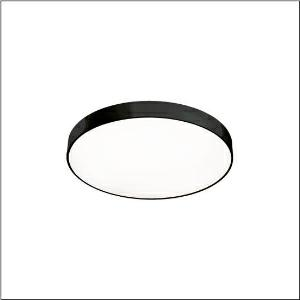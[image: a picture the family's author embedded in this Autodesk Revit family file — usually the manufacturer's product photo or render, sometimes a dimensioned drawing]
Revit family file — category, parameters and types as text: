
# Revit family: round_21_m_51mr36fd0321b
name_source: partatom
category: Lighting Fixtures
units: mm (PartAtom-declared; Revit-internal decimal feet)

## family parameters
Cut with Voids When Loaded = No
Host = Face
Light Source = No
Part Type = Normal
Room Calculation Point = No
Round Connector Dimension = Use Diameter
Shared = No

## types (1)
- Round 21 M (1 x LED, 7500 lm, 54.9 W, 3000K)
    Apparent Load = 55 VA
    CIE Flux Codes = 49 80 96 100 100
    Color Rendering = 80
    Color Temperature = 3000K
    Default Elevation = 1800 mm
    Description = Round 21 M, wall and ceiling luminaire, primary optical cover: cover, of PMMA, opal, light emission: direct distribution, primary light characteristic: symmetric, installation type: suspended mounting, surface-mounted, LED, rated luminous flux: 7.500lm, luminous efficacy: 137lm/W, light colour: 830, colour temperature: 3000K, control gear: DALI 2, with terminal, 5-pole, mains connection: 230V, AC, 50/60Hz, rated input power: 54.8W, housing, of aluminium, coated, black, diameter: 600mm, height: 62mm, protection rating (complete): IP40, insulation class (complete): insulation class I (protective earthing), certification: CE, impact resistance: IK04, permissible operating ambient temperature: -10..+35°C, packaging unit: 1 piece
    Height = 87 mm
    Lamp = 1 x LED
    Lamp Light Flux = 7500 lm
    Lamp Power = 54.9 W
    Lamp count = 1
    Length = 600 mm
    Luminous efficacy = 137 lm/W
    Manufacturer = Siteco
    ModVariant = No
    Model = 51MR36FD0321B
    Mounting Place = Ceiling
    Mounting Type = Surface mounted
    Number of Poles = 1
    OnlyDefault = Yes
    Power Factor = 1
    Product Name = Round 21 M
    Product group = wall and ceiling luminaire | ceiling mounted
    ProductGroupID = 304
    Protection Class = Protection class I
    Protection Degree = IP 40
    RLX_Detail_Level = 1
    RLX_Emergency_Light_Flux = 0 lm
    RLX_Emergency_Type = 0
    RLX_Emergency_Type_DB = No
    RlxData = <blob elided: 17757 chars, md5=d2f81cb6>
    Socket = socket
    Standby Power = 0 W
    System Light Flux = 7500 lm
    System Power = 55 W
    Type Comments = Product without accessories
    Type Image = l_1258332.jpg
    URL = http://relux.com
    VarID = ---
    Voltage = 0 V
    Weight = 0.00 kg
    Width = 0 mm  [stored 0 ft]

note: [stored X ft] marks values corroborated as IEEE doubles in the binary element streams (Revit-internal decimal feet)

## geometry (parser evidence)
native form markers: Blend x4, Sweep x11
no freeform markers — native parametric forms only
